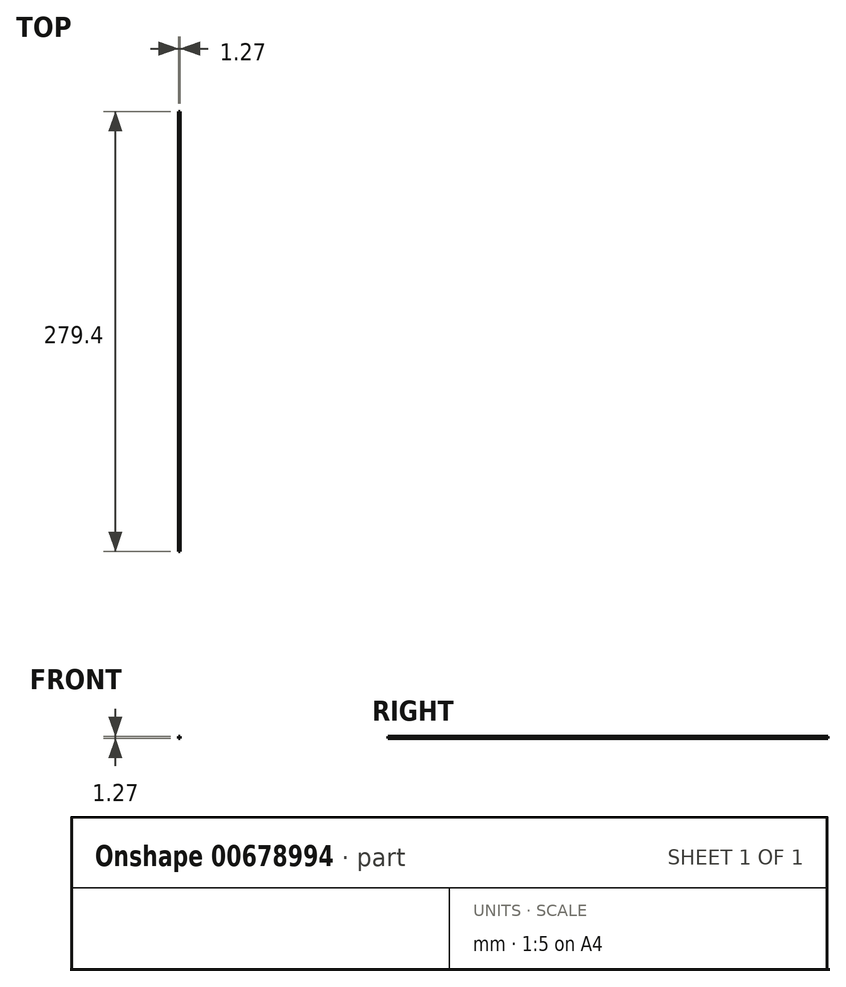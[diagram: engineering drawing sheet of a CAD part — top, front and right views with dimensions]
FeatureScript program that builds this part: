
annotation { "Feature Type Name" : "Feature", "Feature Type Description" : "" }
export const myFeature = defineFeature(function(context is Context, id is Id, definition is map)
    precondition{}
    {
        {
            var Q0;
            Q0=qCreatedBy(makeId("Top.planeOp"),FACE);
            var sketch = newSketch(context, id + "F0", { "sketchPlane" : qUnion([Q0])});
            skLineSegment(sketch, "E0.bottom", {"start": v(-18.85, 240.42) * mm, "end": v(-17.58, 240.42) * mm});
            skLineSegment(sketch, "E0.top", {"start": v(-18.85, -38.98) * mm, "end": v(-17.58, -38.98) * mm});
            skLineSegment(sketch, "E0.left", {"start": v(-18.85, 240.42) * mm, "end": v(-18.85, -38.98) * mm});
            skLineSegment(sketch, "E0.right", {"start": v(-17.58, 240.42) * mm, "end": v(-17.58, -38.98) * mm});
            skSolve(sketch);
        }
        {
            var Q0;
            Q0 = qConstructionFilter(qBodyType(qCreatedBy(id + "F0" ,EDGE), BodyType.WIRE), ConstructionObject.NO);
            extrude(context, id + "F1", {"bodyType" : ToolBodyType.SURFACE, "surfaceEntities" : qUnion([Q0]), "depth" : 1.27 * mm, "offsetDistance" : 25.4 * mm});
        }
    });
